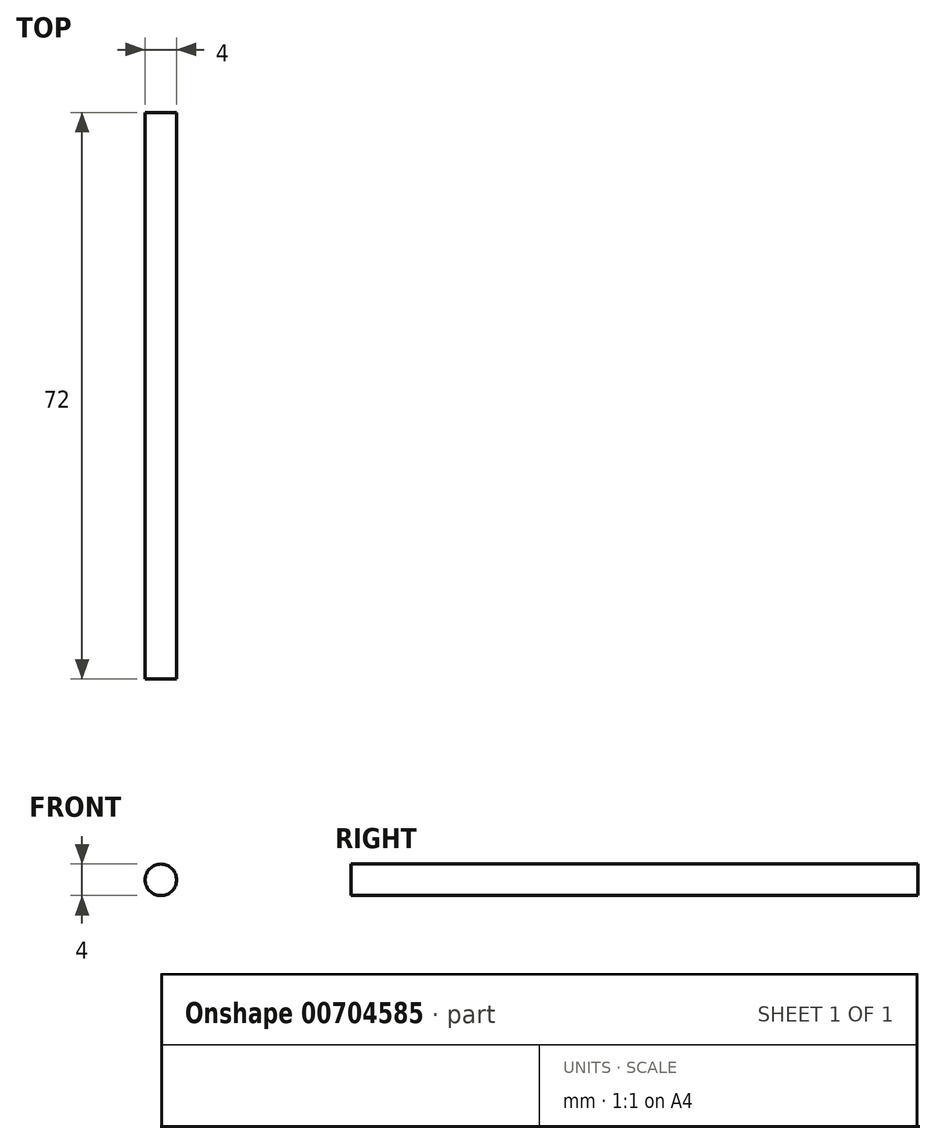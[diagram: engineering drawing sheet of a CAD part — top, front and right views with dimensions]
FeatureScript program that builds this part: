
annotation { "Feature Type Name" : "Feature", "Feature Type Description" : "" }
export const myFeature = defineFeature(function(context is Context, id is Id, definition is map)
    precondition{}
    {
        {
            var Q0;
            Q0=qCreatedBy(makeId("Front.planeOp"),FACE);
            var sketch = newSketch(context, id + "F0", { "sketchPlane" : qUnion([Q0])});
            skCircle(sketch, "E0", {"center": v(0, 0) * mm, "radius": 2 * mm});
            skSolve(sketch);
        }
        {
            var Q0;
            Q0 = qSketchRegion(id + "F0", true);
            extrude(context, id + "F1", {"entities" : qUnion([Q0]), "depth" : 72 * mm, "offsetDistance" : 25 * mm, "symmetric" : true});
        }
    });
